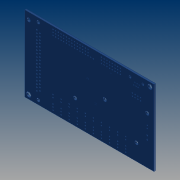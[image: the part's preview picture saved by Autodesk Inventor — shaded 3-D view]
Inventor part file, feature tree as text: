
AUTODESK INVENTOR PART (.ipt)
format: ipt  version: unknown  size: 451,584 bytes
history: native  units: mm (DEFAULTED — no unit token found)
features: plane x3, imported_body x1
ambient origin geometry x5: Origin, X Axis, Y Axis, Z Axis, Center Point
feature tree (4):
  imported_body  "Base1"
  plane  "YZ Plane (RIGHT)"
  plane  "XZ Plane (TOP)"
  plane  "XY Plane (FRONT)"
